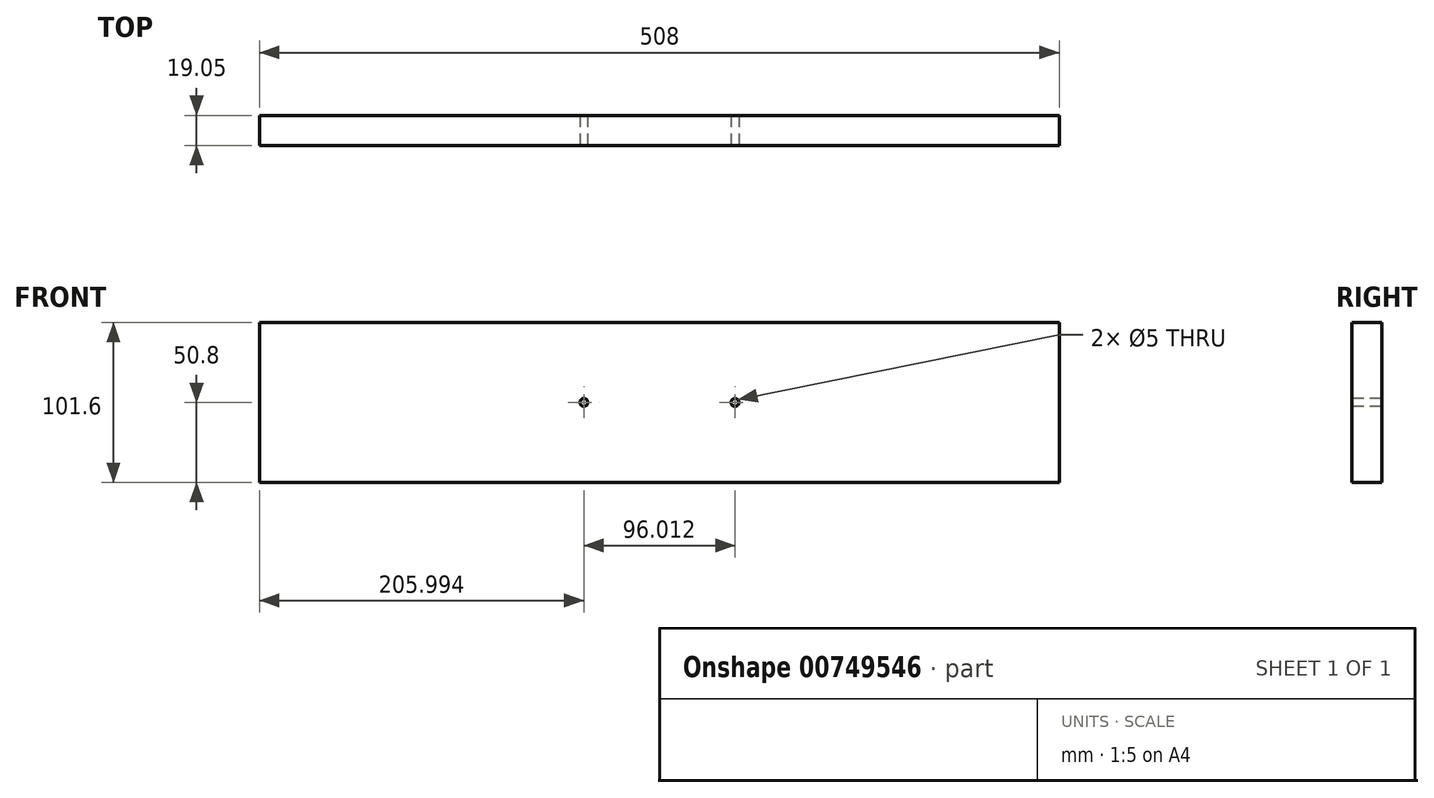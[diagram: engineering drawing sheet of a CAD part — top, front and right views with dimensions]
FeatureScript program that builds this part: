
annotation { "Feature Type Name" : "Feature", "Feature Type Description" : "" }
export const myFeature = defineFeature(function(context is Context, id is Id, definition is map)
    precondition{}
    {
        {
            var Q0;
            Q0=qCreatedBy(makeId("Front.planeOp"),FACE);
            var sketch = newSketch(context, id + "F0", { "sketchPlane" : qUnion([Q0])});
            skLineSegment(sketch, "E0.bottom", {"start": v(-254, 50.8) * mm, "end": v(254, 50.8) * mm});
            skLineSegment(sketch, "E0.top", {"start": v(-254, -50.8) * mm, "end": v(254, -50.8) * mm});
            skLineSegment(sketch, "E0.left", {"start": v(-254, 50.8) * mm, "end": v(-254, -50.8) * mm});
            skLineSegment(sketch, "E0.right", {"start": v(254, 50.8) * mm, "end": v(254, -50.8) * mm});
            skPoint(sketch, "E0.middle", {"position": v(0, 0) * mm});
            skSolve(sketch);
        }
        {
            var Q0;
            Q0=makeQuery(id+"F0.imprint","IMPRINT",FACE,{"disambiguationData":[TD([[makeQuery(id+"F0.imprint","IMPRINT",EDGE,{"derivedFrom":sQuery(id+"F0.wireOp",EDGE,"E0.bottom")}),-1.0]])]});
            extrude(context, id + "F1", {"entities" : qUnion([Q0]), "depth" : 19.05 * mm, "offsetDistance" : 25.4 * mm});
        }
        {
            var Q0;
            Q0=makeQuery(id+"F1.opExtrude","CAP_FACE",FACE,{"disambiguationData":[OSD([sQuery(id+"F0.wireOp",EDGE,"E0.bottom"),sQuery(id+"F0.wireOp",EDGE,"E0.top"),sQuery(id+"F0.wireOp",EDGE,"E0.left"),sQuery(id+"F0.wireOp",EDGE,"E0.right")])],"isStart":false});
            var sketch = newSketch(context, id + "F2", { "sketchPlane" : qUnion([Q0])});
            skLineSegment(sketch, "E1", {"start": v(0, 0) * mm, "end": v(48, 0) * mm});
            skLineSegment(sketch, "E2", {"start": v(0, 0) * mm, "end": v(-48, 0) * mm});
            skPoint(sketch, "E3", {"position": v(-48, 0) * mm});
            skPoint(sketch, "E4", {"position": v(48, 0) * mm});
            skSolve(sketch);
        }
        {
            var Q0;
            Q0=sQuery(id+"F2.wireOp",VERTEX,"E3");
            var Q1;
            Q1=sQuery(id+"F2.wireOp",VERTEX,"E4");
            var Q2;
            Q2=makeQuery(id+"F1.opExtrude","SWEPT_BODY",BODY,{"disambiguationData":[OSD([sQuery(id+"F0.wireOp",EDGE,"E0.bottom"),sQuery(id+"F0.wireOp",EDGE,"E0.top"),sQuery(id+"F0.wireOp",EDGE,"E0.left"),sQuery(id+"F0.wireOp",EDGE,"E0.right")])]});
            hole(context, id + "F3", {"style" : HoleStyle.SIMPLE, "endStyle" : HoleEndStyle.BLIND, "holeDiameter" : 5 * mm, "majorDiameter" : 6.35 * mm, "holeDepth" : 19.05 * mm, "isTappedThrough" : true, "tappedDepth" : 12.7 * mm, "tapClearance" : 3, "startFromSketch" : true, "locations" : qUnion([Q0, Q1]), "scope" : qUnion([Q2])});
        }
    });
